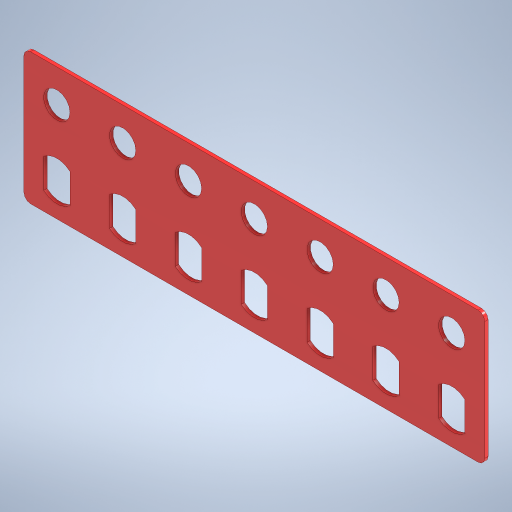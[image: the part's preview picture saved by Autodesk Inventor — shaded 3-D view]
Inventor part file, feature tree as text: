
AUTODESK INVENTOR PART (.ipt)
format: ipt  version: 2024 (Build 280153000, 153)  size: 294,912 bytes
history: native  units: mm
features: extrude x3, fillet x3, sketch x3, pattern_linear x2, other x1
ambient origin geometry x8: Origin, YZ Plane, XZ Plane, XY Plane, X Axis, Y Axis, Z Axis, Center Point
bodies: Body1 (feature_tree)
feature tree (12):
  other  "Těleso1"
  extrude  "Vysunutí1"  Depth=20.0mm
  extrude  "Vysunutí2"  Depth=70.0mm
  pattern_linear  "Obdélníkové pole1"  Spacing1=10.0mm  [1 undecoded]
  fillet  "Zaoblení1"  Radius=10.0mm
  fillet  "Zaoblení2"  Radius=0.5mm
  fillet  "Zaoblení3"  Radius=4.0mm
  extrude  "Vysunutí3"  Depth=5.0mm
  pattern_linear  "Obdélníkové pole2"  Spacing1=5.0mm  [1 undecoded]
  sketch  "Náčrt1"
  sketch  "Náčrt2"
  sketch  "Náčrt3"
note: 2 required parameter values undecoded (feature->parameter linkage not recoverable at this tier; creation-order binding heuristic only, values carry confidence <= 0.55)
